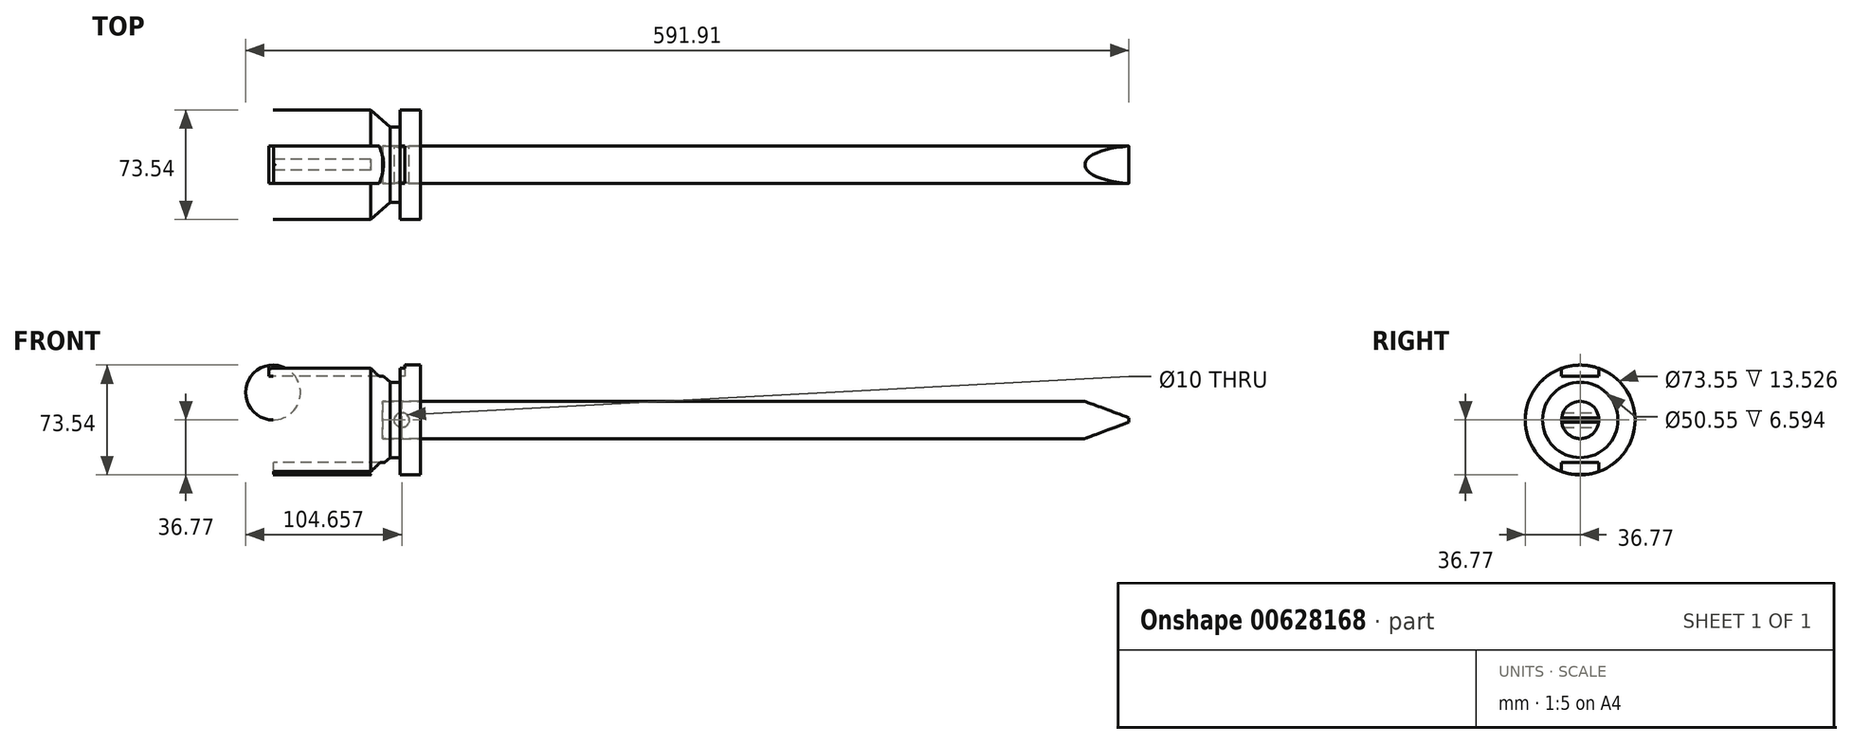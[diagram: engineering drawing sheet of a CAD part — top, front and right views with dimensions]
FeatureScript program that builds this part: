
annotation { "Feature Type Name" : "Feature", "Feature Type Description" : "" }
export const myFeature = defineFeature(function(context is Context, id is Id, definition is map)
    precondition{}
    {
        {
            var Q0;
            Q0=qCreatedBy(makeId("Right.planeOp"),FACE);
            var sketch = newSketch(context, id + "F0", { "sketchPlane" : qUnion([Q0])});
            skCircle(sketch, "E0", {"center": v(0, 0) * mm, "radius": 12.5 * mm});
            skSolve(sketch);
        }
        {
            var Q0;
            Q0=makeQuery(id+"F0.imprint","IMPRINT",FACE,{"disambiguationData":[TD([[makeQuery(id+"F0.imprint","IMPRINT",EDGE,{"derivedFrom":sQuery(id+"F0.wireOp",EDGE,"E0")}),1.0]])]});
            extrude(context, id + "F1", {"entities" : qUnion([Q0]), "oppositeDirection" : true, "depth" : 500 * mm, "offsetDistance" : 25 * mm});
        }
        {
            var Q0;
            Q0=qCreatedBy(makeId("Front.planeOp"),FACE);
            var sketch = newSketch(context, id + "F2", { "sketchPlane" : qUnion([Q0])});
            skCircle(sketch, "E1", {"center": v(-484.6, 0) * mm, "radius": 5 * mm});
            skLineSegment(sketch, "E2", {"start": v(0, 19.5) * mm, "end": v(-30, 19.5) * mm});
            skLineSegment(sketch, "E3", {"start": v(-30, 19.5) * mm, "end": v(-30, 12.64) * mm});
            skLineSegment(sketch, "E4", {"start": v(-30, 12.64) * mm, "end": v(0, 1.5) * mm});
            skLineSegment(sketch, "E5", {"start": v(0, 1.5) * mm, "end": v(0, 19.5) * mm});
            skLineSegment(sketch, "E6", {"start": v(0, 0) * mm, "end": v(0, 1.5) * mm});
            skLineSegment(sketch, "E7", {"start": v(0, 0) * mm, "end": v(0, -1.5) * mm});
            skLineSegment(sketch, "E8", {"start": v(0, -1.5) * mm, "end": v(0, -19.5) * mm});
            skLineSegment(sketch, "E9", {"start": v(-30, -19.5) * mm, "end": v(-30, -12.64) * mm});
            skLineSegment(sketch, "E10", {"start": v(-30, -12.64) * mm, "end": v(0, -1.5) * mm});
            skLineSegment(sketch, "E11", {"start": v(-30, -19.5) * mm, "end": v(0, -19.5) * mm});
            skSolve(sketch);
        }
        {
            var Q0;
            Q0=makeQuery(id+"F2.imprint","IMPRINT",FACE,{"disambiguationData":[TD([[makeQuery(id+"F2.imprint","IMPRINT",EDGE,{"derivedFrom":sQuery(id+"F2.wireOp",EDGE,"E2")}),1.0]])]});
            var Q1;
            Q1=makeQuery(id+"F2.imprint","IMPRINT",FACE,{"disambiguationData":[TD([[makeQuery(id+"F2.imprint","IMPRINT",EDGE,{"derivedFrom":sQuery(id+"F2.wireOp",EDGE,"E8")}),-1.0]])]});
            extrude(context, id + "F3", {"entities" : qUnion([Q0, Q1]), "operationType" : NewBodyOperationType.REMOVE, "endBound" : BoundingType.SYMMETRIC, "oppositeDirection" : true, "depth" : 25 * mm, "offsetDistance" : 25 * mm});
        }
        {
            var Q0;
            Q0=qCreatedBy(makeId("Front.planeOp"),FACE);
            var sketch = newSketch(context, id + "F4", { "sketchPlane" : qUnion([Q0])});
            skCircle(sketch, "E12", {"center": v(-487.25, 0) * mm, "radius": 5 * mm});
            skSolve(sketch);
        }
        {
            var Q0;
            Q0 = qSketchRegion(id + "F4", true);
            extrude(context, id + "F5", {"entities" : qUnion([Q0]), "operationType" : NewBodyOperationType.REMOVE, "endBound" : BoundingType.SYMMETRIC, "depth" : 25 * mm, "offsetDistance" : 25 * mm});
        }
        {
            var Q0;
            Q0=qCreatedBy(makeId("Front.planeOp"),FACE);
            var sketch = newSketch(context, id + "F6", { "sketchPlane" : qUnion([Q0])});
            skLineSegment(sketch, "E13", {"start": v(-474.78, 12.6) * mm, "end": v(-499.97, 12.6) * mm});
            skLineSegment(sketch, "E14", {"start": v(-499.97, 12.6) * mm, "end": v(-499.97, 0) * mm});
            skLineSegment(sketch, "E15", {"start": v(-499.97, 0) * mm, "end": v(-573.52, 0) * mm});
            skArc(sketch, "E16", {"start": v(-573.52, 36.77) * mm, "mid": v(-591.9, 18.39) * mm, "end": v(-573.52, 0) * mm});
            skLineSegment(sketch, "E17", {"start": v(-573.52, 36.77) * mm, "end": v(-508.09, 36.77) * mm});
            skLineSegment(sketch, "E18", {"start": v(-508.09, 36.77) * mm, "end": v(-494.9, 25.28) * mm});
            skLineSegment(sketch, "E19", {"start": v(-494.9, 25.28) * mm, "end": v(-488.3, 25.28) * mm});
            skLineSegment(sketch, "E20", {"start": v(-488.3, 25.28) * mm, "end": v(-488.3, 36.77) * mm});
            skLineSegment(sketch, "E21", {"start": v(-474.78, 12.6) * mm, "end": v(-474.78, 36.77) * mm});
            skLineSegment(sketch, "E22", {"start": v(-474.78, 36.77) * mm, "end": v(-488.3, 36.77) * mm});
            skSolve(sketch);
        }
        {
            var Q0;
            Q0=makeQuery(id+"F6.imprint","IMPRINT",FACE,{"disambiguationData":[TD([[makeQuery(id+"F6.imprint","IMPRINT",EDGE,{"derivedFrom":sQuery(id+"F6.wireOp",EDGE,"E13")}),-1.0]])]});
            var Q1;
            Q1=makeQuery(id+"F1.opExtrude","SWEPT_FACE",FACE,{"disambiguationData":[OSD([sQuery(id+"F0.wireOp",EDGE,"E0")])]});
            revolve(context, id + "F7", {"entities" : qUnion([Q0]), "axis" : qUnion([Q1]), "revolveType" : RevolveType.FULL});
        }
        {
            var Q0;
            Q0=qCreatedBy(makeId("Front.planeOp"),FACE);
            var sketch = newSketch(context, id + "F8", { "sketchPlane" : qUnion([Q0])});
            skLineSegment(sketch, "E23.bottom", {"start": v(-485.14, 37.35) * mm, "end": v(-576.27, 37.35) * mm});
            skLineSegment(sketch, "E23.top", {"start": v(-485.14, 29.35) * mm, "end": v(-576.27, 29.35) * mm});
            skLineSegment(sketch, "E23.left", {"start": v(-485.14, 37.35) * mm, "end": v(-485.14, 29.35) * mm});
            skLineSegment(sketch, "E23.right", {"start": v(-576.27, 37.35) * mm, "end": v(-576.27, 29.35) * mm});
            skLineSegment(sketch, "E24.bottom", {"start": v(-488.3, -36.58) * mm, "end": v(-573.27, -36.58) * mm});
            skLineSegment(sketch, "E24.top", {"start": v(-488.3, -28.58) * mm, "end": v(-573.27, -28.58) * mm});
            skLineSegment(sketch, "E24.left", {"start": v(-488.3, -36.58) * mm, "end": v(-488.3, -28.58) * mm});
            skLineSegment(sketch, "E24.right", {"start": v(-573.27, -36.58) * mm, "end": v(-573.27, -28.58) * mm});
            skSolve(sketch);
        }
        {
            var Q0;
            Q0=makeQuery(id+"F8.imprint","IMPRINT",FACE,{"disambiguationData":[TD([[makeQuery(id+"F8.imprint","IMPRINT",EDGE,{"derivedFrom":sQuery(id+"F8.wireOp",EDGE,"E23.bottom")}),1.0]])]});
            var Q1;
            Q1=makeQuery(id+"F8.imprint","IMPRINT",FACE,{"disambiguationData":[TD([[makeQuery(id+"F8.imprint","IMPRINT",EDGE,{"derivedFrom":sQuery(id+"F8.wireOp",EDGE,"E24.bottom")}),-1.0]])]});
            extrude(context, id + "F9", {"entities" : qUnion([Q0, Q1]), "operationType" : NewBodyOperationType.REMOVE, "endBound" : BoundingType.SYMMETRIC, "depth" : 25 * mm, "offsetDistance" : 25 * mm});
        }
    });
